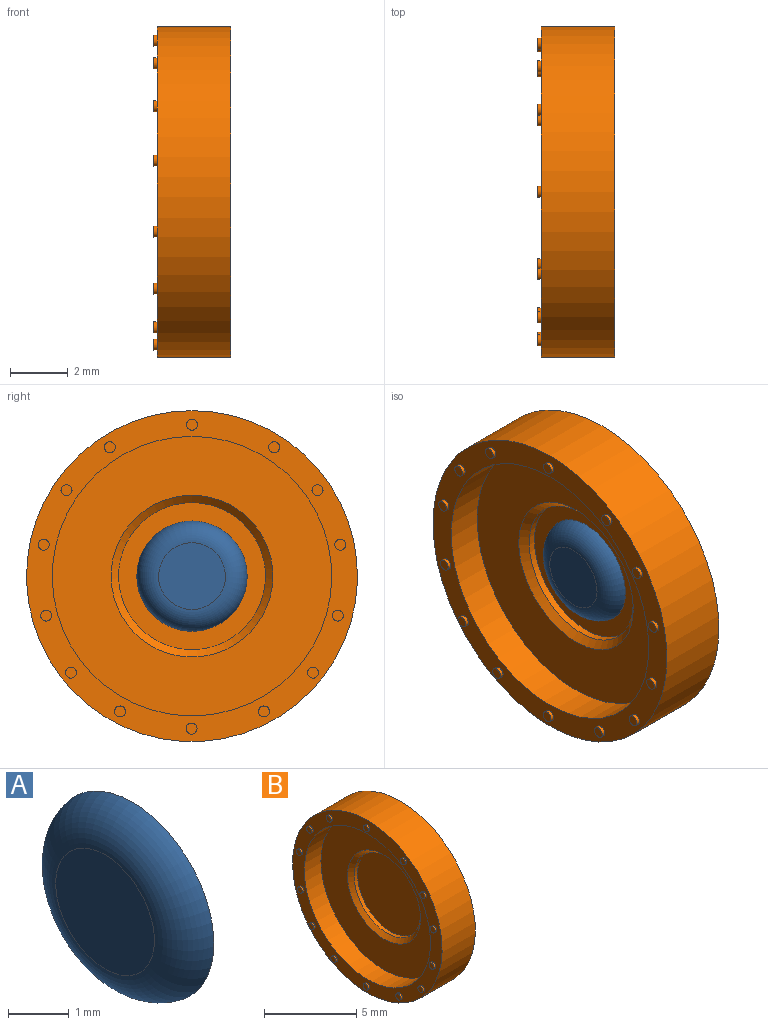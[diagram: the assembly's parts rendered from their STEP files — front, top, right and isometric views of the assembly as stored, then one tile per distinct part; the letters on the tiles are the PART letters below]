
ASSEMBLY  parts=2 mates=1
PART A: 3 faces, bbox 0.8x4.1x4.1 mm
  f0: plane 2.31x2.31mm, normal (-1,0,0), area 4.2mm2, adj f1
  f1: torus R=1.15mm, axis (1,0,0), area 10.8mm2, adj f0,f2
  f2: plane 3.81x3.81mm, normal (1,0,0), area 11.4mm2, adj f1
PART B: 36 faces, bbox 2.7x11.4x11.4 mm
  f0: cylinder r=5.71mm len=11.43mm, axis (1,0,0), area 91.2mm2, adj f1,f2
  f1: plane 11.43x11.43mm, normal (-1,0,0), area 27.8mm2, adj f0,f3,f8,f10,f12,f14,f16,f18
  f2: plane 11.43x11.43mm, normal (1,0,0), area 102.6mm2, adj f0
  f3: cylinder r=4.83mm len=9.65mm, axis (-1,0,0), area 38.5mm2, adj f1,f4
  f4: plane 9.65x9.65mm, normal (-1,0,0), area 48.6mm2, adj f3,f7
  f5: cylinder r=2.54mm len=5.08mm, axis (-1,0,0), area 4.1mm2, adj f6,f7
  f6: plane 5.08x5.08mm, normal (-1,0,0), area 20.3mm2, adj f5
  f7: cone r=2.54mm half-angle=45deg, axis (-1,0,0), area 6mm2, adj f4,f5
  f8: cylinder r=0.19mm len=0.38mm, axis (1,0,0), area 0.2mm2, adj f1,f9
  f9: plane 0.38x0.38mm, normal (-1,0,0), area 0.1mm2, adj f8
  f10: cylinder r=0.19mm len=0.38mm, axis (1,0,0), area 0.2mm2, adj f1,f11
  f11: plane 0.38x0.38mm, normal (-1,0,0), area 0.1mm2, adj f10
  f12: cylinder r=0.19mm len=0.38mm, axis (1,0,0), area 0.2mm2, adj f1,f13
  f13: plane 0.38x0.38mm, normal (-1,0,0), area 0.1mm2, adj f12
  f14: cylinder r=0.19mm len=0.38mm, axis (1,0,0), area 0.2mm2, adj f1,f15
  f15: plane 0.38x0.38mm, normal (-1,0,0), area 0.1mm2, adj f14
  f16: cylinder r=0.19mm len=0.38mm, axis (1,0,0), area 0.2mm2, adj f1,f17
  f17: plane 0.38x0.38mm, normal (-1,0,0), area 0.1mm2, adj f16
  f18: cylinder r=0.19mm len=0.38mm, axis (1,0,0), area 0.2mm2, adj f1,f19
  f19: plane 0.38x0.38mm, normal (-1,0,0), area 0.1mm2, adj f18
  f20: cylinder r=0.19mm len=0.38mm, axis (1,0,0), area 0.2mm2, adj f1,f21
  f21: plane 0.38x0.38mm, normal (-1,0,0), area 0.1mm2, adj f20
  f22: cylinder r=0.19mm len=0.38mm, axis (1,0,0), area 0.2mm2, adj f1,f23
  f23: plane 0.38x0.38mm, normal (-1,0,0), area 0.1mm2, adj f22
  f24: cylinder r=0.19mm len=0.38mm, axis (1,0,0), area 0.2mm2, adj f1,f25
  f25: plane 0.38x0.38mm, normal (-1,0,0), area 0.1mm2, adj f24
  f26: cylinder r=0.19mm len=0.38mm, axis (1,0,0), area 0.2mm2, adj f1,f27
  f27: plane 0.38x0.38mm, normal (-1,0,0), area 0.1mm2, adj f26
  f28: cylinder r=0.19mm len=0.38mm, axis (1,0,0), area 0.2mm2, adj f1,f29
  f29: plane 0.38x0.38mm, normal (-1,0,0), area 0.1mm2, adj f28
  f30: cylinder r=0.19mm len=0.38mm, axis (1,0,0), area 0.2mm2, adj f1,f31
  f31: plane 0.38x0.38mm, normal (-1,0,0), area 0.1mm2, adj f30
  f32: cylinder r=0.19mm len=0.38mm, axis (1,0,0), area 0.2mm2, adj f1,f33
  f33: plane 0.38x0.38mm, normal (-1,0,0), area 0.1mm2, adj f32
  f34: cylinder r=0.19mm len=0.38mm, axis (1,0,0), area 0.2mm2, adj f1,f35
  f35: plane 0.38x0.38mm, normal (-1,0,0), area 0.1mm2, adj f34
PLACE A t=(-24.6,7.86,-46.72)mm
PLACE B t=(-25.1,7.86,-46.72)mm
MATE fastened A.f1 <-> B.f0  axis (1,0,0) through (-43.01,7.86,49.53)mm
